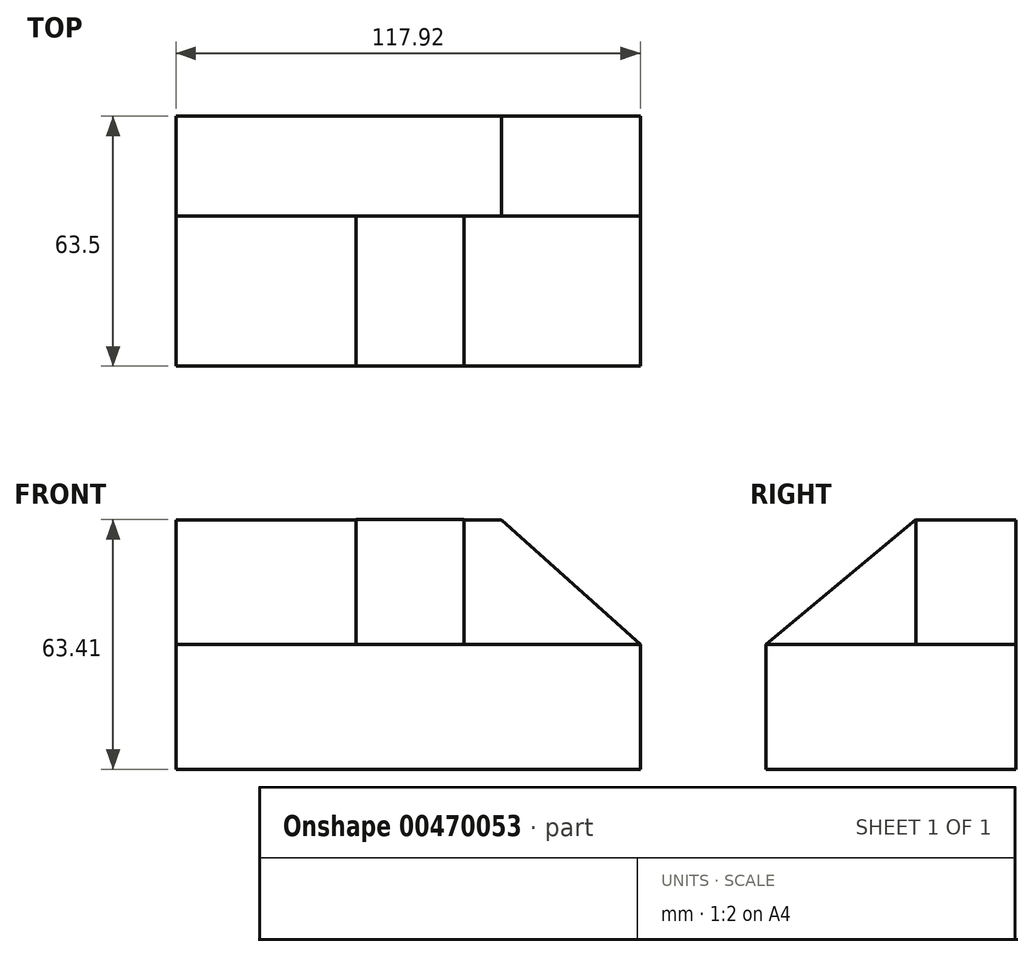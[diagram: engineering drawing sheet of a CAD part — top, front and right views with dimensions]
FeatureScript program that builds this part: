
annotation { "Feature Type Name" : "Feature", "Feature Type Description" : "" }
export const myFeature = defineFeature(function(context is Context, id is Id, definition is map)
    precondition{}
    {
        {
            var Q0;
            Q0=qCreatedBy(makeId("Front.planeOp"),FACE);
            var sketch = newSketch(context, id + "F0", { "sketchPlane" : qUnion([Q0])});
            skLineSegment(sketch, "E0.bottom", {"start": v(23.7, 31.66) * mm, "end": v(-58.96, 31.66) * mm});
            skLineSegment(sketch, "E0.top", {"start": v(58.96, -31.66) * mm, "end": v(-58.96, -31.66) * mm});
            skLineSegment(sketch, "E0.left", {"start": v(58.96, 0) * mm, "end": v(58.96, -31.66) * mm});
            skLineSegment(sketch, "E0.right", {"start": v(-58.96, 31.66) * mm, "end": v(-58.96, -31.66) * mm});
            skPoint(sketch, "E0.middle", {"position": v(0, 0) * mm});
            skLineSegment(sketch, "E1", {"start": v(23.7, 31.66) * mm, "end": v(58.96, 0) * mm});
            skPoint(sketch, "E2.orphan", {"position": v(58.96, 31.66) * mm});
            skLineSegment(sketch, "E3", {"start": v(58.96, 0) * mm, "end": v(-58.96, 0) * mm});
            skSolve(sketch);
        }
        {
            var Q0;
            {var subQ0=sQuery(id+"F0.wireOp",EDGE,"E0.top");Q0=makeQuery(id+"F0.imprint","IMPRINT",FACE,{"disambiguationData":[TD([[makeQuery(id+"F0.imprint","IMPRINT",EDGE,{"derivedFrom":subQ0}),-1.0]])]});}
            extrude(context, id + "F1", {"entities" : qUnion([Q0]), "depth" : 63.5 * mm});
        }
        {
            var Q0;
            {var subQ0=sQuery(id+"F0.wireOp",EDGE,"E0.bottom");Q0=makeQuery(id+"F0.imprint","IMPRINT",FACE,{"disambiguationData":[TD([[makeQuery(id+"F0.imprint","IMPRINT",EDGE,{"derivedFrom":subQ0}),1.0]])]});}
            extrude(context, id + "F2", {"entities" : qUnion([Q0]), "operationType" : NewBodyOperationType.ADD, "depth" : 25.4 * mm});
        }
        {
            var Q0;
            Q0=makeQuery(id+"F1.opExtrude","SWEPT_FACE",FACE,{"disambiguationData":[OSD([sQuery(id+"F0.wireOp",EDGE,"E3")])]});
            var sketch = newSketch(context, id + "F3", { "sketchPlane" : qUnion([Q0])});
            skLineSegment(sketch, "E4", {"start": v(14.22, -25.4) * mm, "end": v(14.22, -63.5) * mm});
            skLineSegment(sketch, "E5", {"start": v(14.22, -63.5) * mm, "end": v(-13.27, -63.5) * mm});
            skLineSegment(sketch, "E6", {"start": v(-13.27, -63.5) * mm, "end": v(-13.27, -25.4) * mm});
            skLineSegment(sketch, "E7", {"start": v(-13.27, -25.4) * mm, "end": v(14.22, -25.4) * mm});
            skSolve(sketch);
        }
        {
            var Q0;
            Q0 = qSketchRegion(id + "F3", true);
            extrude(context, id + "F4", {"entities" : qUnion([Q0]), "operationType" : NewBodyOperationType.ADD, "depth" : 31.75 * mm});
        }
        {
            var Q0;
            Q0=makeQuery(id+"F4.opExtrude","SWEPT_FACE",FACE,{"disambiguationData":[OSD([sQuery(id+"F3.wireOp",EDGE,"E4")])]});
            var sketch = newSketch(context, id + "F5", { "sketchPlane" : qUnion([Q0])});
            skLineSegment(sketch, "E8", {"start": v(-25.4, 31.75) * mm, "end": v(-63.5, 0) * mm});
            skLineSegment(sketch, "E9", {"start": v(-63.5, 0) * mm, "end": v(-63.5, 31.75) * mm});
            skLineSegment(sketch, "E10", {"start": v(-63.5, 31.75) * mm, "end": v(-25.4, 31.75) * mm});
            skSolve(sketch);
        }
        {
            var Q0;
            Q0 = qSketchRegion(id + "F5", true);
            extrude(context, id + "F6", {"entities" : qUnion([Q0]), "operationType" : NewBodyOperationType.REMOVE, "endBound" : BoundingType.THROUGH_ALL, "oppositeDirection" : true, "depth" : 25.4 * mm});
        }
    });
